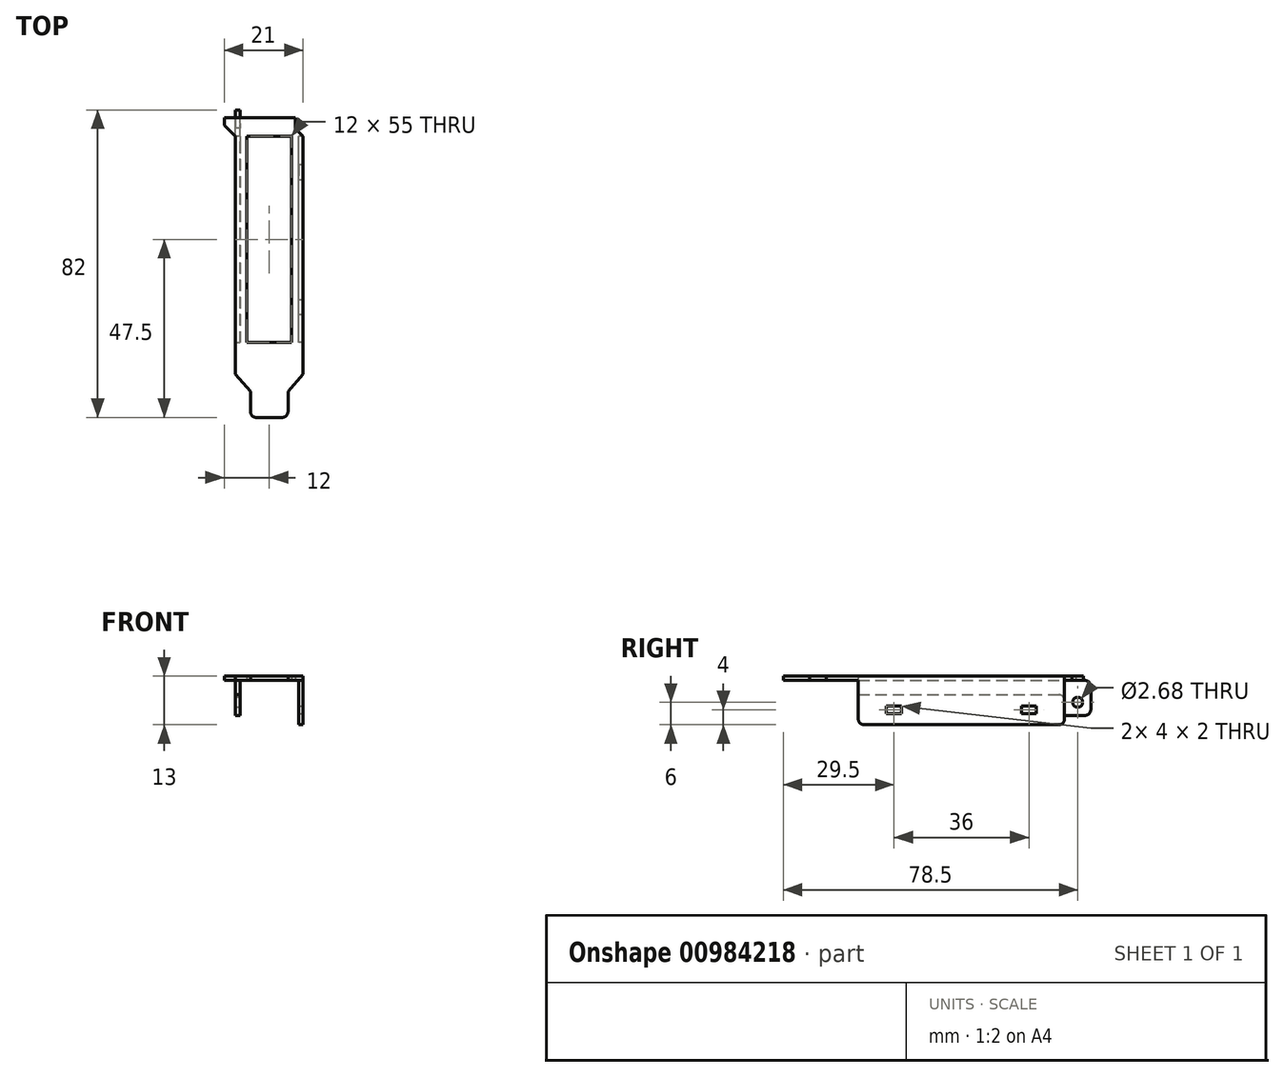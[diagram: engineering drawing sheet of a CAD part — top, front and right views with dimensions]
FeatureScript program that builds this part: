
annotation { "Feature Type Name" : "Feature", "Feature Type Description" : "" }
export const myFeature = defineFeature(function(context is Context, id is Id, definition is map)
    precondition{}
    {
        {
            var Q0;
            Q0=qCreatedBy(makeId("Top.planeOp"),FACE);
            var sketch = newSketch(context, id + "F0", { "sketchPlane" : qUnion([Q0])});
            skLineSegment(sketch, "E0.bottom", {"start": v(0, 0) * mm, "end": v(18, 0) * mm});
            skLineSegment(sketch, "E0.top", {"start": v(0, 63.5) * mm, "end": v(18, 63.5) * mm});
            skLineSegment(sketch, "E0.left", {"start": v(0, 0) * mm, "end": v(0, 63.5) * mm});
            skLineSegment(sketch, "E0.right", {"start": v(18, 0) * mm, "end": v(18, 63.5) * mm});
            skLineSegment(sketch, "E1", {"start": v(0, 0) * mm, "end": v(4, -4.5) * mm});
            skLineSegment(sketch, "E2", {"start": v(4, -4.5) * mm, "end": v(4, -11.5) * mm});
            skLineSegment(sketch, "E3", {"start": v(4, -11.5) * mm, "end": v(14, -11.5) * mm});
            skLineSegment(sketch, "E4", {"start": v(14, -11.5) * mm, "end": v(14, -4.5) * mm});
            skLineSegment(sketch, "E5", {"start": v(14, -4.5) * mm, "end": v(18, 0) * mm});
            skLineSegment(sketch, "E6", {"start": v(0, 63.5) * mm, "end": v(-3, 66.5) * mm});
            skLineSegment(sketch, "E7", {"start": v(-3, 66.5) * mm, "end": v(-3, 68.5) * mm});
            skLineSegment(sketch, "E8", {"start": v(-3, 68.5) * mm, "end": v(16, 68.5) * mm});
            skLineSegment(sketch, "E9", {"start": v(16, 68.5) * mm, "end": v(16, 65.5) * mm});
            skLineSegment(sketch, "E10", {"start": v(16, 65.5) * mm, "end": v(18, 63.5) * mm});
            skPoint(sketch, "E11", {"position": v(9, -11.5) * mm});
            skPoint(sketch, "E12", {"position": v(9, 63.5) * mm});
            skLineSegment(sketch, "E13.bottom", {"start": v(3, 8.5) * mm, "end": v(15, 8.5) * mm});
            skLineSegment(sketch, "E13.top", {"start": v(3, 63.5) * mm, "end": v(15, 63.5) * mm});
            skLineSegment(sketch, "E13.left", {"start": v(3, 8.5) * mm, "end": v(3, 63.5) * mm});
            skLineSegment(sketch, "E13.right", {"start": v(15, 8.5) * mm, "end": v(15, 63.5) * mm});
            skPoint(sketch, "E14", {"position": v(24.22, 60.6) * mm});
            skSolve(sketch);
        }
        {
            var Q0;
            Q0 = qSketchRegion(id + "F0", true);
            extrude(context, id + "F1", {"entities" : qUnion([Q0]), "depth" : 1.2 * mm, "offsetDistance" : 25 * mm});
        }
        {
            var Q0;
            Q0=makeQuery(id+"F1.opExtrude","CAP_FACE",FACE,{"disambiguationData":[OSD([sQuery(id+"F0.wireOp",EDGE,"E0.left"),sQuery(id+"F0.wireOp",EDGE,"E0.right"),sQuery(id+"F0.wireOp",EDGE,"E1"),sQuery(id+"F0.wireOp",EDGE,"E2"),sQuery(id+"F0.wireOp",EDGE,"E3"),sQuery(id+"F0.wireOp",EDGE,"E4"),sQuery(id+"F0.wireOp",EDGE,"E5"),sQuery(id+"F0.wireOp",EDGE,"E6"),sQuery(id+"F0.wireOp",EDGE,"E7"),sQuery(id+"F0.wireOp",EDGE,"E8"),sQuery(id+"F0.wireOp",EDGE,"E9"),sQuery(id+"F0.wireOp",EDGE,"E10"),sQuery(id+"F0.wireOp",EDGE,"E13.bottom"),sQuery(id+"F0.wireOp",EDGE,"E13.top"),sQuery(id+"F0.wireOp",EDGE,"E13.left"),sQuery(id+"F0.wireOp",EDGE,"E13.right")])],"isStart":true});
            var sketch = newSketch(context, id + "F2", { "sketchPlane" : qUnion([Q0])});
            skLineSegment(sketch, "E15.bottom", {"start": v(18, -8.5) * mm, "end": v(16.8, -8.5) * mm});
            skLineSegment(sketch, "E15.top", {"start": v(18, -63.5) * mm, "end": v(16.8, -63.5) * mm});
            skLineSegment(sketch, "E15.left", {"start": v(18, -8.5) * mm, "end": v(18, -63.5) * mm});
            skLineSegment(sketch, "E15.right", {"start": v(16.8, -8.5) * mm, "end": v(16.8, -63.5) * mm});
            skPoint(sketch, "E16", {"position": v(16.8, -36) * mm});
            skPoint(sketch, "E17", {"position": v(15, -36) * mm});
            skLineSegment(sketch, "E18.bottom", {"start": v(0, -8.5) * mm, "end": v(1.2, -8.5) * mm});
            skLineSegment(sketch, "E18.top", {"start": v(0, -70.5) * mm, "end": v(1.2, -70.5) * mm});
            skLineSegment(sketch, "E18.left", {"start": v(0, -8.5) * mm, "end": v(0, -70.5) * mm});
            skLineSegment(sketch, "E18.right", {"start": v(1.2, -8.5) * mm, "end": v(1.2, -70.5) * mm});
            skSolve(sketch);
        }
        {
            var Q0;
            Q0=makeQuery(id+"F2.imprint","IMPRINT",FACE,{"disambiguationData":[TD([[makeQuery(id+"F2.imprint","IMPRINT",EDGE,{"derivedFrom":sQuery(id+"F2.wireOp",EDGE,"E15.bottom")}),1.0]])]});
            extrude(context, id + "F3", {"entities" : qUnion([Q0]), "operationType" : NewBodyOperationType.ADD, "depth" : (13 - 1.2) * mm, "offsetDistance" : 25 * mm});
        }
        {
            var Q0;
            Q0=makeQuery(id+"F3.boolean.opBoolean","MERGE",FACE,{"derivedFrom":[makeQuery(id+"F1.opExtrude","SWEPT_FACE",FACE,{"disambiguationData":[OSD([sQuery(id+"F0.wireOp",EDGE,"E0.right")])]}),makeQuery(id+"F3.opExtrude","SWEPT_FACE",FACE,{"disambiguationData":[OSD([sQuery(id+"F2.wireOp",EDGE,"E15.left")])]})]});
            var sketch = newSketch(context, id + "F4", { "sketchPlane" : qUnion([Q0])});
            skLineSegment(sketch, "E19", {"start": v(36, -11.8) * mm, "end": v(36, -8.59) * mm});
            skPoint(sketch, "E20.oppositeSnap0", {"position": v(8.5, -8.8) * mm});
            skLineSegment(sketch, "E20.bottom", {"start": v(16, -6.8) * mm, "end": v(20, -6.8) * mm});
            skLineSegment(sketch, "E20.top", {"start": v(16, -8.8) * mm, "end": v(20, -8.8) * mm});
            skLineSegment(sketch, "E20.left", {"start": v(16, -6.8) * mm, "end": v(16, -8.8) * mm});
            skLineSegment(sketch, "E20.right", {"start": v(20, -6.8) * mm, "end": v(20, -8.8) * mm});
            skLineSegment(sketch, "E21.MirrorCS", {"start": v(52, -6.8) * mm, "end": v(52, -8.8) * mm});
            skLineSegment(sketch, "E22.MirrorCS", {"start": v(56, -6.8) * mm, "end": v(52, -6.8) * mm});
            skLineSegment(sketch, "E23.MirrorCS", {"start": v(56, -6.8) * mm, "end": v(56, -8.8) * mm});
            skLineSegment(sketch, "E24.MirrorCS", {"start": v(56, -8.8) * mm, "end": v(52, -8.8) * mm});
            skSolve(sketch);
        }
        {
            var Q0;
            Q0 = qSketchRegion(id + "F4", true);
            extrude(context, id + "F5", {"entities" : qUnion([Q0]), "operationType" : NewBodyOperationType.REMOVE, "oppositeDirection" : true, "depth" : 25 * mm, "offsetDistance" : 25 * mm});
        }
        {
            var Q0;
            {var subQ4=sQuery(id+"F2.wireOp",EDGE,"E18.bottom");Q0=makeQuery(id+"F2.imprint","IMPRINT",FACE,{"disambiguationData":[TD([[makeQuery(id+"F2.imprint","IMPRINT",EDGE,{"derivedFrom":subQ4}),-1.0]])]});}
            var Q1;
            {var subQ0=sQuery(id+"F2.wireOp",EDGE,"E18.top");Q1=makeQuery(id+"F2.imprint","IMPRINT",FACE,{"disambiguationData":[TD([[makeQuery(id+"F2.imprint","IMPRINT",EDGE,{"derivedFrom":subQ0}),1.0]])]});}
            extrude(context, id + "F6", {"entities" : qUnion([Q0, Q1]), "operationType" : NewBodyOperationType.ADD, "depth" : (10.5 - 1.2) * mm, "offsetDistance" : 25 * mm});
        }
        {
            var Q0;
            Q0=makeQuery(id+"F6.boolean.opBoolean","MERGE",FACE,{"derivedFrom":[makeQuery(id+"F1.opExtrude","SWEPT_FACE",FACE,{"disambiguationData":[OSD([sQuery(id+"F0.wireOp",EDGE,"E0.left")])]}),makeQuery(id+"F6.opExtrude","SWEPT_FACE",FACE,{"disambiguationData":[OSD([sQuery(id+"F2.wireOp",EDGE,"E18.left")])]})]});
            var sketch = newSketch(context, id + "F7", { "sketchPlane" : qUnion([Q0])});
            skLineSegment(sketch, "E25.bottom", {"start": v(-8.5, -9.3) * mm, "end": v(-63.5, -9.3) * mm});
            skLineSegment(sketch, "E25.top", {"start": v(-8.5, -3.8) * mm, "end": v(-63.5, -3.8) * mm});
            skLineSegment(sketch, "E25.left", {"start": v(-8.5, -9.3) * mm, "end": v(-8.5, -3.8) * mm});
            skLineSegment(sketch, "E25.right", {"start": v(-63.5, -9.3) * mm, "end": v(-63.5, -3.8) * mm});
            skCircle(sketch, "E26", {"center": v(-67, -5.8) * mm, "radius": 1.34 * mm});
            skSolve(sketch);
        }
        {
            var Q0;
            Q0 = qSketchRegion(id + "F7", true);
            extrude(context, id + "F8", {"entities" : qUnion([Q0]), "operationType" : NewBodyOperationType.REMOVE, "oppositeDirection" : true, "depth" : 5 * mm, "offsetDistance" : 25 * mm});
        }
        {
            var Q0;
            Q0=makeQuery(id+"F1.opExtrude","CAP_FACE",FACE,{"disambiguationData":[OSD([sQuery(id+"F0.wireOp",EDGE,"E0.left"),sQuery(id+"F0.wireOp",EDGE,"E0.right"),sQuery(id+"F0.wireOp",EDGE,"E1"),sQuery(id+"F0.wireOp",EDGE,"E2"),sQuery(id+"F0.wireOp",EDGE,"E3"),sQuery(id+"F0.wireOp",EDGE,"E4"),sQuery(id+"F0.wireOp",EDGE,"E5"),sQuery(id+"F0.wireOp",EDGE,"E6"),sQuery(id+"F0.wireOp",EDGE,"E7"),sQuery(id+"F0.wireOp",EDGE,"E8"),sQuery(id+"F0.wireOp",EDGE,"E9"),sQuery(id+"F0.wireOp",EDGE,"E10"),sQuery(id+"F0.wireOp",EDGE,"E13.bottom"),sQuery(id+"F0.wireOp",EDGE,"E13.top"),sQuery(id+"F0.wireOp",EDGE,"E13.left"),sQuery(id+"F0.wireOp",EDGE,"E13.right")])],"isStart":false});
            var sketch = newSketch(context, id + "F9", { "sketchPlane" : qUnion([Q0])});
            skLineSegment(sketch, "E27.bottom", {"start": v(-3, 68.5) * mm, "end": v(16, 68.5) * mm});
            skLineSegment(sketch, "E27.top", {"start": v(-3, 67.3) * mm, "end": v(16, 67.3) * mm});
            skLineSegment(sketch, "E27.left", {"start": v(-3, 68.5) * mm, "end": v(-3, 67.3) * mm});
            skLineSegment(sketch, "E27.right", {"start": v(16, 68.5) * mm, "end": v(16, 67.3) * mm});
            skSolve(sketch);
        }
        {
            var Q0;
            Q0=makeQuery(id+"FCfRnbjY4mfaOiM_1.boolean.opBoolean","MERGE",FACE,{"derivedFrom":[makeQuery(id+"F1.opExtrude","SWEPT_FACE",FACE,{"disambiguationData":[OSD([sQuery(id+"F0.wireOp",EDGE,"E8")])]}),makeQuery(id+"FCfRnbjY4mfaOiM_1.opExtrude","SWEPT_FACE",FACE,{"disambiguationData":[OSD([sQuery(id+"F9.wireOp",EDGE,"E27.bottom")])]})]});
            var sketch = newSketch(context, id + "F10", { "sketchPlane" : qUnion([Q0])});
            skCircle(sketch, "E28", {"center": v(-1.25, 0.6) * mm, "radius": 2.25 * mm});
            skPoint(sketch, "E28.centerSnap0", {"position": v(3, 0.6) * mm});
            skLineSegment(sketch, "E29", {"start": v(-1.25, -1.65) * mm, "end": v(3, -1.65) * mm});
            skLineSegment(sketch, "E30", {"start": v(-1.25, 2.85) * mm, "end": v(3, 2.85) * mm});
            skSolve(sketch);
        }
        {
            var Q0;
            Q0=makeQuery(id+"F6.opExtrude","CAP_EDGE",EDGE,{"disambiguationData":[OSD([sQuery(id+"F2.wireOp",EDGE,"E18.top")])],"isStart":false});
            var Q1;
            Q1=makeQuery(id+"F8.boolean.opBoolean","COPY",EDGE,{"derivedFrom":makeQuery(id+"F8.opExtrude","SWEPT_EDGE",EDGE,{"disambiguationData":[OSD([sQuery(id+"F2.wireOp",EDGE,"E18.left"),sQuery(id+"F7.wireOp",EDGE,"E25.bottom"),sQuery(id+"F7.wireOp",EDGE,"E25.right")])]})});
            var Q2;
            Q2=makeQuery(id+"F8.boolean.opBoolean","COPY",EDGE,{"derivedFrom":makeQuery(id+"F8.opExtrude","SWEPT_EDGE",EDGE,{"disambiguationData":[OSD([sQuery(id+"F0.wireOp",EDGE,"E0.left"),sQuery(id+"F2.wireOp",EDGE,"E18.bottom"),sQuery(id+"F2.wireOp",EDGE,"E18.left"),sQuery(id+"F7.wireOp",EDGE,"E25.top"),sQuery(id+"F7.wireOp",EDGE,"E25.left")])]})});
            var Q3;
            Q3=makeQuery(id+"F3.opExtrude","CAP_EDGE",EDGE,{"disambiguationData":[OSD([sQuery(id+"F2.wireOp",EDGE,"E15.bottom")])],"isStart":false});
            var Q4;
            Q4=makeQuery(id+"F3.opExtrude","CAP_EDGE",EDGE,{"disambiguationData":[OSD([sQuery(id+"F2.wireOp",EDGE,"E15.top")])],"isStart":false});
            var Q5;
            Q5=makeQuery(id+"F1.opExtrude","SWEPT_EDGE",EDGE,{"disambiguationData":[OSD([sQuery(id+"F0.wireOp",EDGE,"E2"),sQuery(id+"F0.wireOp",EDGE,"E3")])]});
            var Q6;
            Q6=makeQuery(id+"F1.opExtrude","SWEPT_EDGE",EDGE,{"disambiguationData":[OSD([sQuery(id+"F0.wireOp",EDGE,"E3"),sQuery(id+"F0.wireOp",EDGE,"E4")])]});
            var Q7;
            Q7=makeQuery(id+"FCfRnbjY4mfaOiM_1.opExtrude","CAP_EDGE",EDGE,{"disambiguationData":[OSD([sQuery(id+"F9.wireOp",EDGE,"E27.left")])],"isStart":false});
            var Q8;
            Q8=makeQuery(id+"FCfRnbjY4mfaOiM_1.opExtrude","CAP_EDGE",EDGE,{"disambiguationData":[OSD([sQuery(id+"F9.wireOp",EDGE,"E27.right")])],"isStart":false});
            var Q9;
            Q9=makeQuery(id+"FAvVRW4UygIGI7b_1.boolean.opBoolean","COPY",EDGE,{"derivedFrom":makeQuery(id+"FAvVRW4UygIGI7b_1.opExtrude","SWEPT_EDGE",EDGE,{"disambiguationData":[OSD([sQuery(id+"F0.wireOp",EDGE,"E7"),sQuery(id+"F0.wireOp",EDGE,"E8"),sQuery(id+"F9.wireOp",EDGE,"E27.bottom"),sQuery(id+"F9.wireOp",EDGE,"E27.left"),sQuery(id+"F10.wireOp",EDGE,"E30")])]})});
            var Q10;
            Q10=makeQuery(id+"FAvVRW4UygIGI7b_1.boolean.opBoolean","COPY",EDGE,{"derivedFrom":makeQuery(id+"FAvVRW4UygIGI7b_1.opExtrude","SWEPT_EDGE",EDGE,{"disambiguationData":[OSD([sQuery(id+"F0.wireOp",EDGE,"E7"),sQuery(id+"F0.wireOp",EDGE,"E8"),sQuery(id+"F9.wireOp",EDGE,"E27.bottom"),sQuery(id+"F9.wireOp",EDGE,"E27.left"),sQuery(id+"F10.wireOp",EDGE,"E29")])]})});
            var Q11;
            Q11=makeQuery(id+"F6.opExtrude","CAP_EDGE",EDGE,{"disambiguationData":[OSD([sQuery(id+"F2.wireOp",EDGE,"E18.top")])],"isStart":true});
            var Q12;
            Q12=makeQuery(id+"F8.boolean.opBoolean","COPY",EDGE,{"derivedFrom":makeQuery(id+"F8.opExtrude","SWEPT_EDGE",EDGE,{"disambiguationData":[OSD([sQuery(id+"F7.wireOp",EDGE,"E25.top"),sQuery(id+"F7.wireOp",EDGE,"E25.right")])]})});
            fillet(context, id + "F11", {"entities" : qUnion([Q0, Q1, Q2, Q3, Q4, Q5, Q6, Q7, Q8, Q9, Q10, Q11, Q12]), "radius" : 1.5 * mm, "tangentPropagation" : true, "allowEdgeOverflow" : false});
        }
    });
